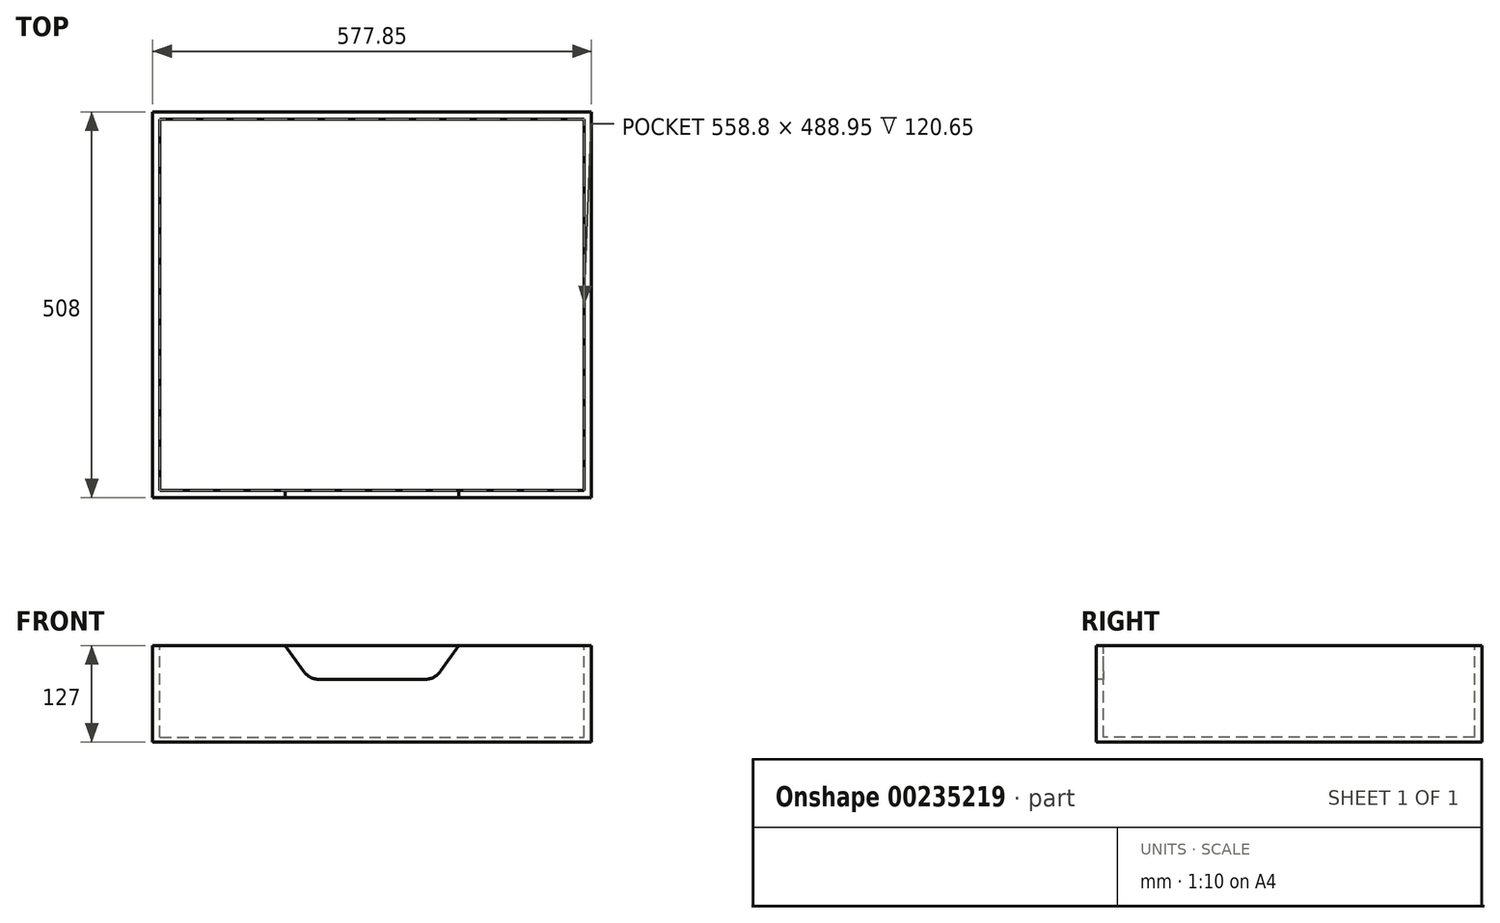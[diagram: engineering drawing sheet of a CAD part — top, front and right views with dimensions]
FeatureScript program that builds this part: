
annotation { "Feature Type Name" : "Feature", "Feature Type Description" : "" }
export const myFeature = defineFeature(function(context is Context, id is Id, definition is map)
    precondition{}
    {
        {
            var Q0;
            Q0=qCreatedBy(makeId("Top.planeOp"),FACE);
            var sketch = newSketch(context, id + "F0", { "sketchPlane" : qUnion([Q0])});
            skLineSegment(sketch, "E0.bottom", {"start": v(0, 0) * mm, "end": v(577.85, 0) * mm});
            skLineSegment(sketch, "E0.top", {"start": v(0, -508) * mm, "end": v(577.85, -508) * mm});
            skLineSegment(sketch, "E0.left", {"start": v(0, 0) * mm, "end": v(0, -508) * mm});
            skLineSegment(sketch, "E0.right", {"start": v(577.85, 0) * mm, "end": v(577.85, -508) * mm});
            skSolve(sketch);
        }
        {
            var Q0;
            Q0 = qSketchRegion(id + "F0", true);
            extrude(context, id + "F1", {"entities" : qUnion([Q0]), "depth" : 127 * mm});
        }
        {
            var Q0;
            Q0=makeQuery(id+"F1.opExtrude","CAP_FACE",FACE,{"disambiguationData":[OSD([sQuery(id+"F0.wireOp",EDGE,"E0.bottom"),sQuery(id+"F0.wireOp",EDGE,"E0.top"),sQuery(id+"F0.wireOp",EDGE,"E0.left"),sQuery(id+"F0.wireOp",EDGE,"E0.right")])],"isStart":false});
            var sketch = newSketch(context, id + "F2", { "sketchPlane" : qUnion([Q0])});
            skLineSegment(sketch, "E1.0", {"start": v(9.53, -9.53) * mm, "end": v(9.53, -498.48) * mm});
            skLineSegment(sketch, "E1.1", {"start": v(568.33, -9.53) * mm, "end": v(9.53, -9.53) * mm});
            skLineSegment(sketch, "E1.2", {"start": v(568.33, -498.48) * mm, "end": v(568.33, -9.53) * mm});
            skLineSegment(sketch, "E1.3", {"start": v(9.53, -498.48) * mm, "end": v(568.33, -498.48) * mm});
            skSolve(sketch);
        }
        {
            var Q0;
            Q0=makeQuery(id+"F2.imprint","IMPRINT",FACE,{"disambiguationData":[TD([[makeQuery(id+"F2.imprint","IMPRINT",EDGE,{"derivedFrom":sQuery(id+"F2.wireOp",EDGE,"E1.0")}),1.0]])]});
            extrude(context, id + "F3", {"entities" : qUnion([Q0]), "operationType" : NewBodyOperationType.REMOVE, "oppositeDirection" : true, "depth" : 120.65 * mm});
        }
        {
            var Q0;
            Q0=makeQuery(id+"F1.opExtrude","SWEPT_FACE",FACE,{"disambiguationData":[OSD([sQuery(id+"F0.wireOp",EDGE,"E0.top")])]});
            var sketch = newSketch(context, id + "F4", { "sketchPlane" : qUnion([Q0])});
            skLineSegment(sketch, "E2", {"start": v(288.93, 127) * mm, "end": v(288.93, 0) * mm, "construction": true});
            skLineSegment(sketch, "E3", {"start": v(174.62, 127) * mm, "end": v(206.38, 82.55) * mm});
            skLineSegment(sketch, "E4", {"start": v(206.38, 82.55) * mm, "end": v(371.48, 82.55) * mm});
            skLineSegment(sketch, "E5", {"start": v(371.48, 82.55) * mm, "end": v(403.23, 127) * mm});
            skLineSegment(sketch, "E6", {"start": v(403.23, 127) * mm, "end": v(174.63, 127) * mm});
            skSolve(sketch);
        }
        {
            var Q0;
            Q0=makeQuery(id+"F4.imprint","IMPRINT",FACE,{"disambiguationData":[TD([[makeQuery(id+"F4.imprint","IMPRINT",EDGE,{"derivedFrom":sQuery(id+"F4.wireOp",EDGE,"E3")}),1.0]])]});
            extrude(context, id + "F5", {"entities" : qUnion([Q0]), "operationType" : NewBodyOperationType.REMOVE, "endBound" : BoundingType.UP_TO_NEXT, "oppositeDirection" : true, "depth" : 25.4 * mm});
        }
        {
            var Q0;
            Q0=makeQuery(id+"F5.boolean.opBoolean","COPY",EDGE,{"derivedFrom":makeQuery(id+"F5.opExtrude","SWEPT_EDGE",EDGE,{"disambiguationData":[OSD([sQuery(id+"F0.wireOp",EDGE,"E0.top"),sQuery(id+"F4.wireOp",EDGE,"E5"),sQuery(id+"F4.wireOp",EDGE,"E6")])]})});
            var Q1;
            Q1=makeQuery(id+"F5.boolean.opBoolean","COPY",EDGE,{"derivedFrom":makeQuery(id+"F5.opExtrude","SWEPT_EDGE",EDGE,{"disambiguationData":[OSD([sQuery(id+"F4.wireOp",EDGE,"E4"),sQuery(id+"F4.wireOp",EDGE,"E5")])]})});
            var Q2;
            Q2=makeQuery(id+"F5.boolean.opBoolean","COPY",EDGE,{"derivedFrom":makeQuery(id+"F5.opExtrude","SWEPT_EDGE",EDGE,{"disambiguationData":[OSD([sQuery(id+"F0.wireOp",EDGE,"E0.top"),sQuery(id+"F4.wireOp",EDGE,"E3"),sQuery(id+"F4.wireOp",EDGE,"E6")])]})});
            var Q3;
            Q3=makeQuery(id+"F5.boolean.opBoolean","COPY",EDGE,{"derivedFrom":makeQuery(id+"F5.opExtrude","SWEPT_EDGE",EDGE,{"disambiguationData":[OSD([sQuery(id+"F4.wireOp",EDGE,"E3"),sQuery(id+"F4.wireOp",EDGE,"E4")])]})});
            fillet(context, id + "F6", {"entities" : qUnion([Q0, Q1, Q2, Q3]), "radius" : 25.4 * mm, "tangentPropagation" : true, "allowEdgeOverflow" : false});
        }
    });
